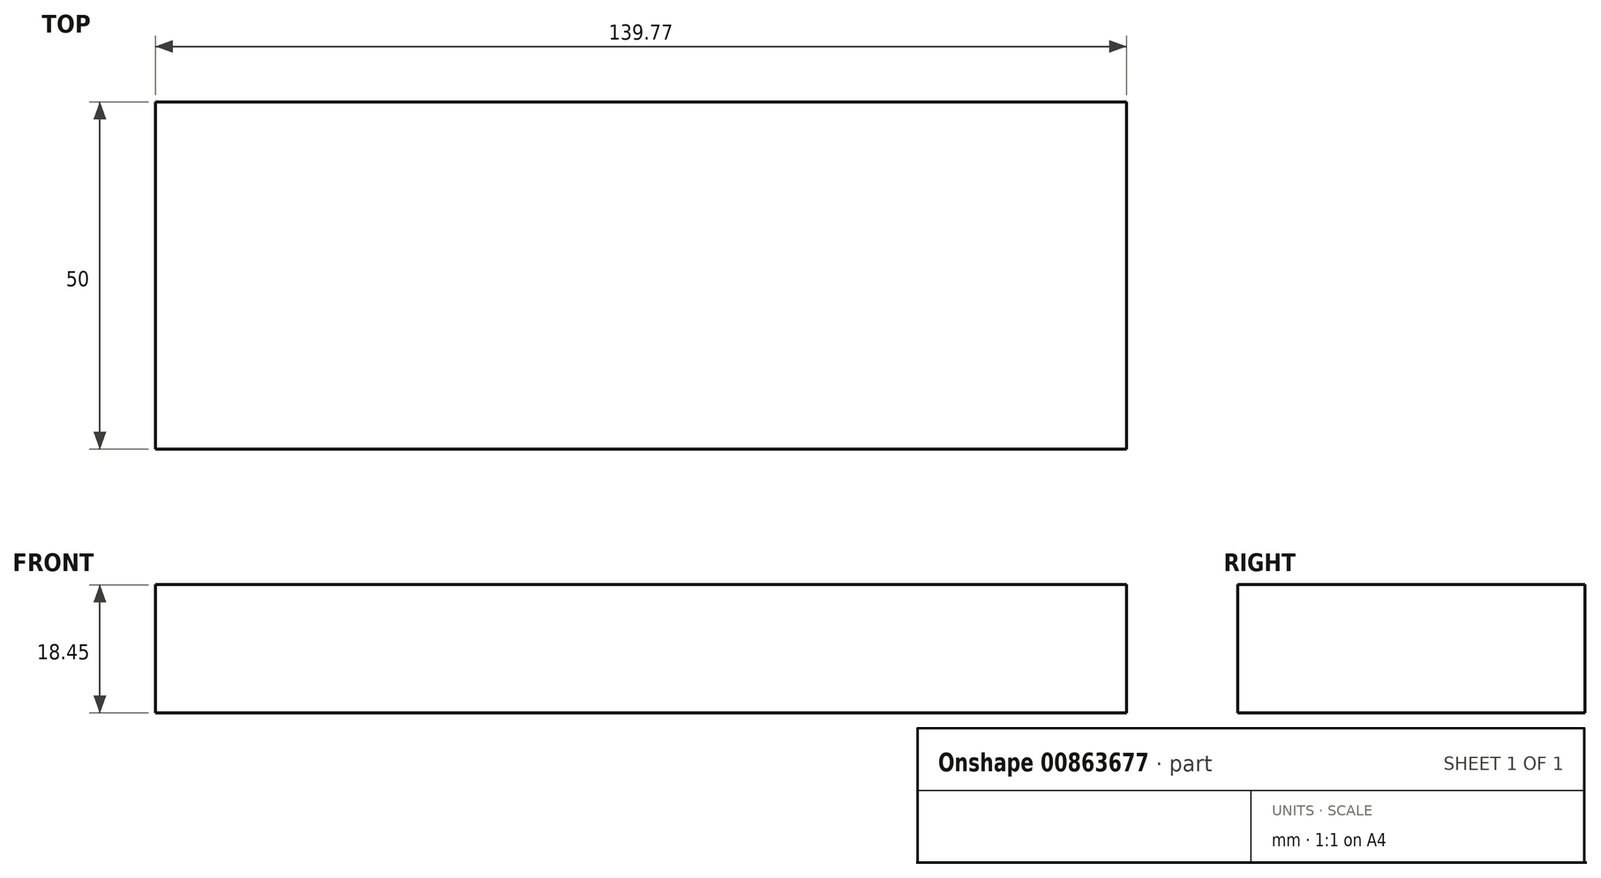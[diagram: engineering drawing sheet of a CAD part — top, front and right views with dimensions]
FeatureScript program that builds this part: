
annotation { "Feature Type Name" : "Feature", "Feature Type Description" : "" }
export const myFeature = defineFeature(function(context is Context, id is Id, definition is map)
    precondition{}
    {
        {
            var Q0;
            Q0=qCreatedBy(makeId("Front.planeOp"),FACE);
            var sketch = newSketch(context, id + "F0", { "sketchPlane" : qUnion([Q0])});
            skLineSegment(sketch, "E0.bottom", {"start": v(-68.54, 35.24) * mm, "end": v(71.23, 35.24) * mm});
            skLineSegment(sketch, "E0.top", {"start": v(-68.54, 16.79) * mm, "end": v(71.23, 16.79) * mm});
            skLineSegment(sketch, "E0.left", {"start": v(-68.54, 35.24) * mm, "end": v(-68.54, 16.79) * mm});
            skLineSegment(sketch, "E0.right", {"start": v(71.23, 35.24) * mm, "end": v(71.23, 16.79) * mm});
            skSolve(sketch);
        }
        {
            var Q0;
            Q0 = qSketchRegion(id + "F0", true);
            extrude(context, id + "F1", {"entities" : qUnion([Q0]), "oppositeDirection" : true, "depth" : 50 * mm, "hasOffset" : true, "offsetDistance" : 25.4 * mm, "offsetOppositeDirection" : true});
        }
    });
